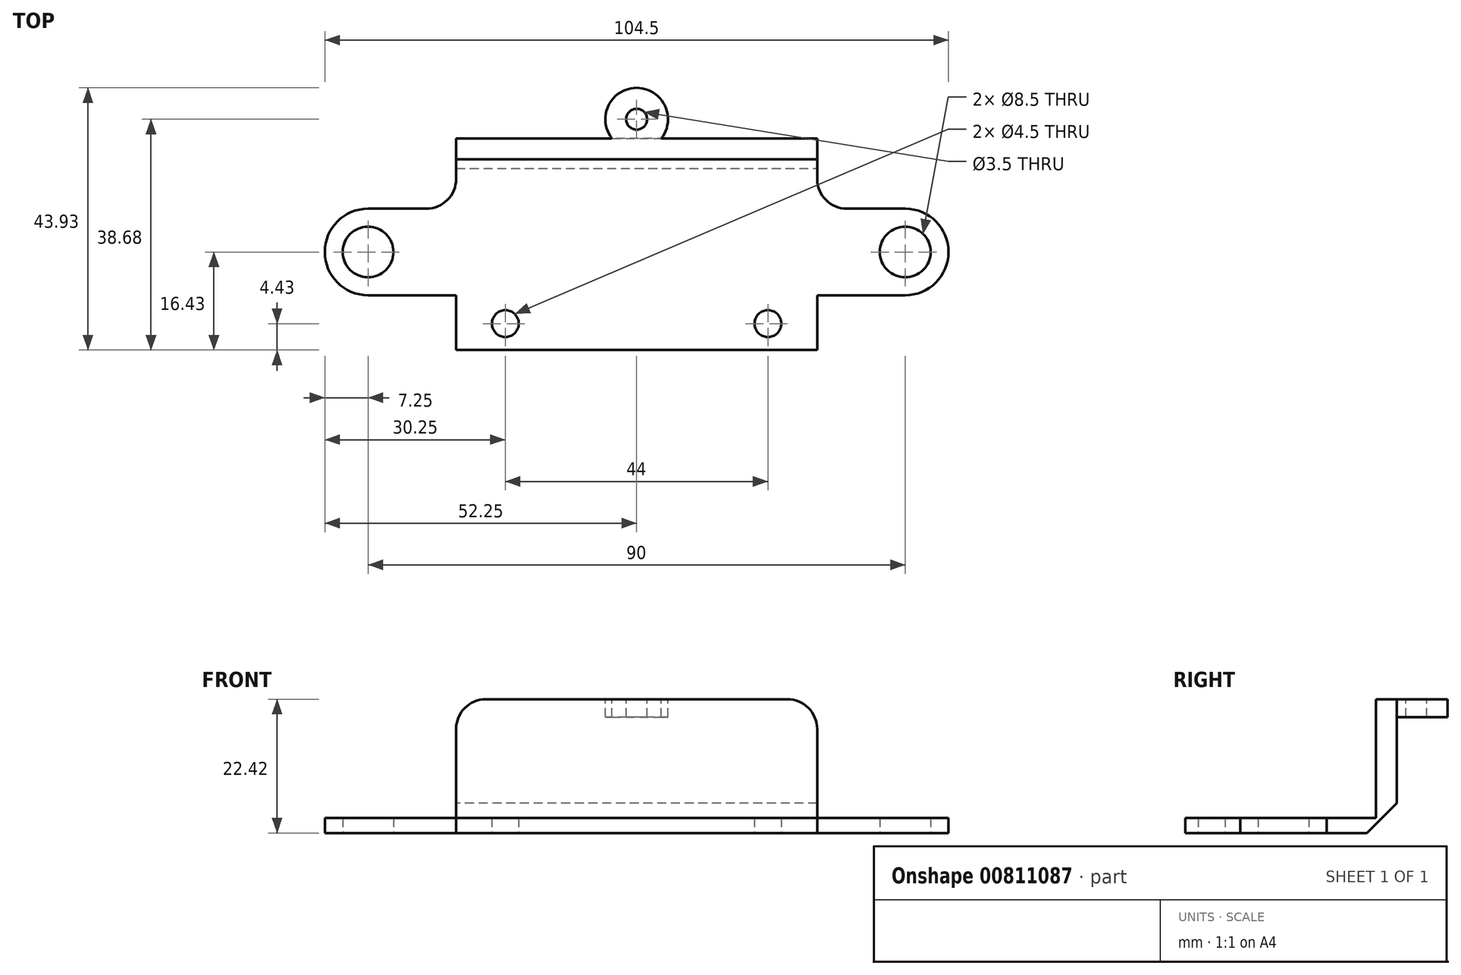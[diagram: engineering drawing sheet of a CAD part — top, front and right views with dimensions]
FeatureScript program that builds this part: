
annotation { "Feature Type Name" : "Feature", "Feature Type Description" : "" }
export const myFeature = defineFeature(function(context is Context, id is Id, definition is map)
    precondition{}
    {
        {
            var Q0;
            Q0=qCreatedBy(makeId("Top.planeOp"),FACE);
            var sketch = newSketch(context, id + "F0", { "sketchPlane" : qUnion([Q0])});
            skCircle(sketch, "E0", {"center": v(-45, 0) * mm, "radius": 4.25 * mm});
            skArc(sketch, "E1.0", {"start": v(-45, 7.25) * mm, "mid": v(-52.25, 0) * mm, "end": v(-45, -7.25) * mm});
            skLineSegment(sketch, "E2.bottom", {"start": v(-45, 7.25) * mm, "end": v(-30.24, 7.25) * mm});
            skLineSegment(sketch, "E2.top", {"start": v(-45, -7.25) * mm, "end": v(-30.24, -7.25) * mm});
            skLineSegment(sketch, "E2.left", {"start": v(-45, -7.25) * mm, "end": v(-45, -7.25) * mm});
            skLineSegment(sketch, "E3.bottom", {"start": v(-30.24, -16.43) * mm, "end": v(0, -16.43) * mm});
            skLineSegment(sketch, "E3.top", {"start": v(-30.24, 19) * mm, "end": v(0, 19) * mm});
            skLineSegment(sketch, "E3.left", {"start": v(-30.24, -16.43) * mm, "end": v(-30.24, -7.25) * mm});
            skLineSegment(sketch, "E3.right", {"start": v(0, -16.43) * mm, "end": v(0, 19) * mm});
            skLineSegment(sketch, "E4.trimOffspring", {"start": v(-30.24, 7.25) * mm, "end": v(-30.24, 19) * mm});
            skSolve(sketch);
        }
        {
            var Q0;
            Q0=makeQuery(id+"F0.imprint","IMPRINT",FACE,{"disambiguationData":[TD([[makeQuery(id+"F0.imprint","IMPRINT",EDGE,{"derivedFrom":sQuery(id+"F0.wireOp",EDGE,"E0")}),-1.0]])]});
            extrude(context, id + "F1", {"entities" : qUnion([Q0]), "depth" : 2.5 * mm, "offsetDistance" : 25 * mm});
        }
        {
            var Q0;
            Q0=makeQuery(id+"F1.opExtrude","CAP_FACE",FACE,{"disambiguationData":[OSD([sQuery(id+"F0.wireOp",EDGE,"E0"),sQuery(id+"F0.wireOp",EDGE,"E1.0"),sQuery(id+"F0.wireOp",EDGE,"E2.bottom"),sQuery(id+"F0.wireOp",EDGE,"E2.top"),sQuery(id+"F0.wireOp",EDGE,"E3.bottom"),sQuery(id+"F0.wireOp",EDGE,"E3.top"),sQuery(id+"F0.wireOp",EDGE,"E3.left"),sQuery(id+"F0.wireOp",EDGE,"E3.right"),sQuery(id+"F0.wireOp",EDGE,"E4.trimOffspring")])],"isStart":false});
            var sketch = newSketch(context, id + "F2", { "sketchPlane" : qUnion([Q0])});
            skLineSegment(sketch, "E5.0", {"start": v(-30.24, 19) * mm, "end": v(0, 19) * mm});
            skLineSegment(sketch, "E6.top", {"start": v(-30.24, 15.5) * mm, "end": v(0, 15.5) * mm});
            skLineSegment(sketch, "E6.left", {"start": v(-30.24, 19) * mm, "end": v(-30.24, 15.5) * mm});
            skLineSegment(sketch, "E6.right", {"start": v(0, 19) * mm, "end": v(0, 15.5) * mm});
            skSolve(sketch);
        }
        {
            var Q0;
            Q0=makeQuery(id+"F2.imprint","IMPRINT",FACE,{"disambiguationData":[TD([[makeQuery(id+"F2.imprint","IMPRINT",EDGE,{"derivedFrom":sQuery(id+"F2.wireOp",EDGE,"E5.0")}),-1.0]])]});
            extrude(context, id + "F3", {"entities" : qUnion([Q0]), "operationType" : NewBodyOperationType.ADD, "depth" : (23.92 - 4) * mm, "offsetDistance" : 25 * mm});
        }
        {
            var Q0;
            Q0=makeQuery(id+"F1.opExtrude","SWEPT_BODY",BODY,{"disambiguationData":[OSD([sQuery(id+"F0.wireOp",EDGE,"E0"),sQuery(id+"F0.wireOp",EDGE,"E1.0"),sQuery(id+"F0.wireOp",EDGE,"E2.bottom"),sQuery(id+"F0.wireOp",EDGE,"E2.top"),sQuery(id+"F0.wireOp",EDGE,"E3.bottom"),sQuery(id+"F0.wireOp",EDGE,"E3.top"),sQuery(id+"F0.wireOp",EDGE,"E3.left"),sQuery(id+"F0.wireOp",EDGE,"E3.right"),sQuery(id+"F0.wireOp",EDGE,"E4.trimOffspring")])]});
            var Q1;
            Q1=qCreatedBy(makeId("Right.planeOp"),FACE);
            mirror(context, id + "F4", {"operationType" : NewBodyOperationType.ADD, "entities" : qUnion([Q0]), "mirrorPlane" : qUnion([Q1])});
        }
        {
            var Q0;
            {var subQ0=makeQuery(id+"F3.opExtrude","CAP_FACE",FACE,{"disambiguationData":[OSD([sQuery(id+"F2.wireOp",EDGE,"E5.0"),sQuery(id+"F2.wireOp",EDGE,"E6.top"),sQuery(id+"F2.wireOp",EDGE,"E6.left"),sQuery(id+"F2.wireOp",EDGE,"E6.right")])],"isStart":false});Q0=makeQuery(id+"F4.boolean.opBoolean","MERGE",FACE,{"derivedFrom":[subQ0,makeQuery(id+"F4.opPattern","COPY",FACE,{"derivedFrom":subQ0,"instanceName":"1"})]});}
            var sketch = newSketch(context, id + "F5", { "sketchPlane" : qUnion([Q0])});
            skCircle(sketch, "E7", {"center": v(0, 22.25) * mm, "radius": 1.75 * mm});
            skCircle(sketch, "E8.0", {"center": v(0, 22.25) * mm, "radius": 5.25 * mm});
            skSolve(sketch);
        }
        {
            var Q0;
            Q0=makeQuery(id+"F5.imprint","IMPRINT",FACE,{"disambiguationData":[TD([[makeQuery(id+"F5.imprint","IMPRINT",EDGE,{"derivedFrom":sQuery(id+"F5.wireOp",EDGE,"E7")}),-1.0]])]});
            extrude(context, id + "F6", {"entities" : qUnion([Q0]), "operationType" : NewBodyOperationType.ADD, "oppositeDirection" : true, "depth" : 3 * mm, "offsetDistance" : 25 * mm});
        }
        {
            var Q0;
            {var subQ0=makeQuery(id+"F1.opExtrude","CAP_FACE",FACE,{"disambiguationData":[OSD([sQuery(id+"F0.wireOp",EDGE,"E0"),sQuery(id+"F0.wireOp",EDGE,"E1.0"),sQuery(id+"F0.wireOp",EDGE,"E2.bottom"),sQuery(id+"F0.wireOp",EDGE,"E2.top"),sQuery(id+"F0.wireOp",EDGE,"E3.bottom"),sQuery(id+"F0.wireOp",EDGE,"E3.top"),sQuery(id+"F0.wireOp",EDGE,"E3.left"),sQuery(id+"F0.wireOp",EDGE,"E3.right"),sQuery(id+"F0.wireOp",EDGE,"E4.trimOffspring")])],"isStart":true});Q0=makeQuery(id+"F4.boolean.opBoolean","MERGE",FACE,{"derivedFrom":[subQ0,makeQuery(id+"F4.opPattern","COPY",FACE,{"derivedFrom":subQ0,"instanceName":"1"})]});}
            var sketch = newSketch(context, id + "F7", { "sketchPlane" : qUnion([Q0])});
            skPoint(sketch, "E9", {"position": v(-22, 12) * mm});
            skPoint(sketch, "E10.MirrorP", {"position": v(22, 12) * mm});
            skSolve(sketch);
        }
        {
            var Q0;
            Q0=sQuery(id+"F7.wireOp",VERTEX,"E9");
            var Q1;
            Q1=sQuery(id+"F7.wireOp",VERTEX,"E10.MirrorP");
            var Q2;
            Q2=makeQuery(id+"F1.opExtrude","SWEPT_BODY",BODY,{"disambiguationData":[OSD([sQuery(id+"F0.wireOp",EDGE,"E0"),sQuery(id+"F0.wireOp",EDGE,"E1.0"),sQuery(id+"F0.wireOp",EDGE,"E2.bottom"),sQuery(id+"F0.wireOp",EDGE,"E2.top"),sQuery(id+"F0.wireOp",EDGE,"E3.bottom"),sQuery(id+"F0.wireOp",EDGE,"E3.top"),sQuery(id+"F0.wireOp",EDGE,"E3.left"),sQuery(id+"F0.wireOp",EDGE,"E3.right"),sQuery(id+"F0.wireOp",EDGE,"E4.trimOffspring")])]});
            hole(context, id + "F8", {"style" : HoleStyle.SIMPLE, "endStyle" : HoleEndStyle.THROUGH, "standardTappedOrClearance" : lookupTablePath({ "standard" : "ANSI", "fit" : "Normal (ASME)", "size" : "#8", "type" : "Clearance" }), "standardBlindInLast" : lookupTablePath({ "fit" : "Free", "standard" : "ANSI", "size" : "#8", "type" : "Clearance" }), "holeDiameter" : 4.5 * mm, "majorDiameter" : 5 * mm, "tappedDepth" : 12 * mm, "tapClearance" : 3, "startFromSketch" : true, "locations" : qUnion([Q0, Q1]), "scope" : qUnion([Q2])});
        }
        {
            var Q0;
            Q0=makeQuery(id+"F4.opPattern","COPY",EDGE,{"derivedFrom":makeQuery(id+"F1.opExtrude","SWEPT_EDGE",EDGE,{"disambiguationData":[OSD([sQuery(id+"F0.wireOp",EDGE,"E2.bottom"),sQuery(id+"F0.wireOp",EDGE,"E4.trimOffspring")])]}),"instanceName":"1"});
            var Q1;
            Q1=makeQuery(id+"F1.opExtrude","SWEPT_EDGE",EDGE,{"disambiguationData":[OSD([sQuery(id+"F0.wireOp",EDGE,"E2.bottom"),sQuery(id+"F0.wireOp",EDGE,"E4.trimOffspring")])]});
            var Q2;
            {var subQ0=sQuery(id+"F5.wireOp",EDGE,"E8.0");var subQ1=sQuery(id+"F2.wireOp",EDGE,"E5.0");var subQ2=makeQuery(id+"F3.opExtrude","CAP_EDGE",EDGE,{"disambiguationData":[OSD([subQ1])],"isStart":false});Q2=makeQuery(id+"F6.opExtrude","SWEPT_EDGE",EDGE,{"disambiguationData":[OSD([subQ1,subQ0]),TDD([makeQuery(id+"F5.imprint","INTERSECT",VERTEX,{"disambiguationData":[OD(0.0)],"derivedFrom":[makeQuery(id+"F4.boolean.opBoolean","MERGE",EDGE,{"derivedFrom":[subQ2,makeQuery(id+"F4.opPattern","COPY",EDGE,{"derivedFrom":subQ2,"instanceName":"1"})]}),subQ0]})])]});}
            var Q3;
            {var subQ0=sQuery(id+"F5.wireOp",EDGE,"E8.0");var subQ1=sQuery(id+"F2.wireOp",EDGE,"E5.0");var subQ2=makeQuery(id+"F3.opExtrude","CAP_EDGE",EDGE,{"disambiguationData":[OSD([subQ1])],"isStart":false});Q3=makeQuery(id+"F6.opExtrude","SWEPT_EDGE",EDGE,{"disambiguationData":[OSD([subQ1,subQ0]),TDD([makeQuery(id+"F5.imprint","INTERSECT",VERTEX,{"disambiguationData":[OD(1.0)],"derivedFrom":[makeQuery(id+"F4.boolean.opBoolean","MERGE",EDGE,{"derivedFrom":[subQ2,makeQuery(id+"F4.opPattern","COPY",EDGE,{"derivedFrom":subQ2,"instanceName":"1"})]}),subQ0]})])]});}
            var Q4;
            Q4=makeQuery(id+"F3.opExtrude","CAP_EDGE",EDGE,{"disambiguationData":[OSD([sQuery(id+"F2.wireOp",EDGE,"E6.left")])],"isStart":false});
            var Q5;
            Q5=makeQuery(id+"F4.opPattern","COPY",EDGE,{"derivedFrom":makeQuery(id+"F3.opExtrude","CAP_EDGE",EDGE,{"disambiguationData":[OSD([sQuery(id+"F2.wireOp",EDGE,"E6.left")])],"isStart":false}),"instanceName":"1"});
            fillet(context, id + "F9", {"entities" : qUnion([Q0, Q1, Q2, Q3, Q4, Q5]), "radius" : 5 * mm, "tangentPropagation" : true, "allowEdgeOverflow" : false});
        }
        {
            var Q0;
            {var subQ0=makeQuery(id+"F1.opExtrude","CAP_EDGE",EDGE,{"disambiguationData":[OSD([sQuery(id+"F0.wireOp",EDGE,"E3.top")])],"isStart":true});Q0=makeQuery(id+"F4.boolean.opBoolean","MERGE",EDGE,{"derivedFrom":[subQ0,makeQuery(id+"F4.opPattern","COPY",EDGE,{"derivedFrom":subQ0,"instanceName":"1"})]});}
            var Q1;
            {var subQ0=makeQuery(id+"F3.opExtrude","CAP_EDGE",EDGE,{"disambiguationData":[OSD([sQuery(id+"F2.wireOp",EDGE,"E6.top")])],"isStart":true});Q1=makeQuery(id+"F4.boolean.opBoolean","MERGE",EDGE,{"derivedFrom":[subQ0,makeQuery(id+"F4.opPattern","COPY",EDGE,{"derivedFrom":subQ0,"instanceName":"1"})]});}
            chamfer(context, id + "F10", {"entities" : qUnion([Q0, Q1]), "width" : 5 * mm, "tangentPropagation" : true});
        }
    });
